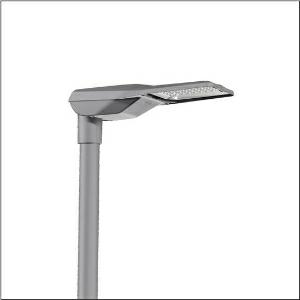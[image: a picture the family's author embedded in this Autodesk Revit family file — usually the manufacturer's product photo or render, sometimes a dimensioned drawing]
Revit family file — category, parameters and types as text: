
# Revit family: streetlight_sl_21_iq_mini___p0_8a_5xe2u31d08hb_de2c
name_source: partatom
category: Lighting Fixtures
units: mm (PartAtom-declared; Revit-internal decimal feet)

## family parameters
Cut with Voids When Loaded = No
Host = Face
Light Source = No
Part Type = Normal
Room Calculation Point = No
Round Connector Dimension = Use Diameter
Shared = No

## types (1)
- --- (1 x LED, 9540 lm, 70.9 W, 3000K)
    Apparent Load = 71 VA
    CIE Flux Codes = 33 69 96 100 100
    Color Rendering = 70
    Color Temperature = 3000K
    Default Elevation = 1800 mm
    Description = Streetlight SL 21 iQ mini, mast luminaire, primary light control with lens, of PMMA, primary optical cover: cover, of toughened safety glass, transparent, light distribution: P0.8a, light emission: direct distribution, primary light characteristic: asymmetric, installation type: post-top, side-entry, LED, High Power LED, rated luminous flux: 9.540lm, luminous efficacy: 135lm/W, light colour: 730, colour temperature: 3000K, control gear: iQ-Comfort, control: pre-setting: linear dimming characteristic, Auto-Match, Temp-Guard, Lumen-Switch, Night-Set, Smart-Wire, Light-Fading, Desk-Remote (wireless, voltage-free reading and setting of iQ features in the workshop via application-optimized NFC function/RFID function), optimised constant luminous flux control (CLO 2.0), mains connection: 220..240V, AC, 50/60Hz, start of lifetime: 71W, end of service life: 75W, reduction: 31W, luminaire housing, of diecast aluminium, powder-coated, Siteco® metallic grey (DB 702S), corrosivity category C5 mid according to DIN EN ISO 12944, please order mast flange separately, inclination adjustable: 0°, 5°, 10°, 15°, sealing non-destructively replaceable, multi-level sealing system, length: 628mm, width: 235mm, height: 110mm, mast flange for spigot size: 42mm (side-entry): 5XC10008XM4, 60/48mm (side-entry/post-top): 5XC10108XM2, 76/60mm (side-entry/post-top): 5XC10108XM1, mounting height: 4..8m, protection rating (complete): IP66, insulation class (complete): insulation class II (safety insulation), certification: CE, ENEC, ENEC+, VDE, impact resistance: IK09, permissible operating ambient temperature for outdoor applications: -40..+50°C, standard-compliant lighting for roads and squares, packaging unit: 1 piece

Light Distribution: P0.8a
    Height = 110 mm
    Lamp = 1 x LED
    Lamp Light Flux = 9540 lm
    Lamp Power = 70.9 W
    Lamp count = 1
    Length = 625 mm
    Luminous efficacy = 135 lm/W
    Manufacturer = Siteco
    ModVariant = No
    Model = 5XE2U31D08HB
    Number of Poles = 1
    OnlyDefault = Yes
    Power Factor = 1
    Product Name = Streetlight SL 21 iQ mini | P0.8a
    Product group = mast luminaire | pylon top
    ProductGroupID = 6100
    Protection Class = Protection class II
    Protection Degree = IP 66
    RLX_Detail_Level = 1
    RLX_Emergency_Light_Flux = 0 lm
    RLX_Emergency_Type = 0
    RLX_Emergency_Type_DB = No
    RlxData = <blob elided: 91977 chars, md5=5257fe70>
    Socket = socket
    Standby Power = 0 W
    System Light Flux = 9540 lm
    System Power = 71 W
    Type Comments = factory setting: luminous flux: 100 % | dim-lin: 254 | 711 mA
    Type Image = l_1003519.jpg
    URL = http://relux.com
    VarID = @adj_069408
    Voltage = 0 V
    Weight = 0.00 kg
    Width = 234 mm

## geometry (parser evidence)
native form markers: Blend x4, Sweep x11
no freeform markers — native parametric forms only
